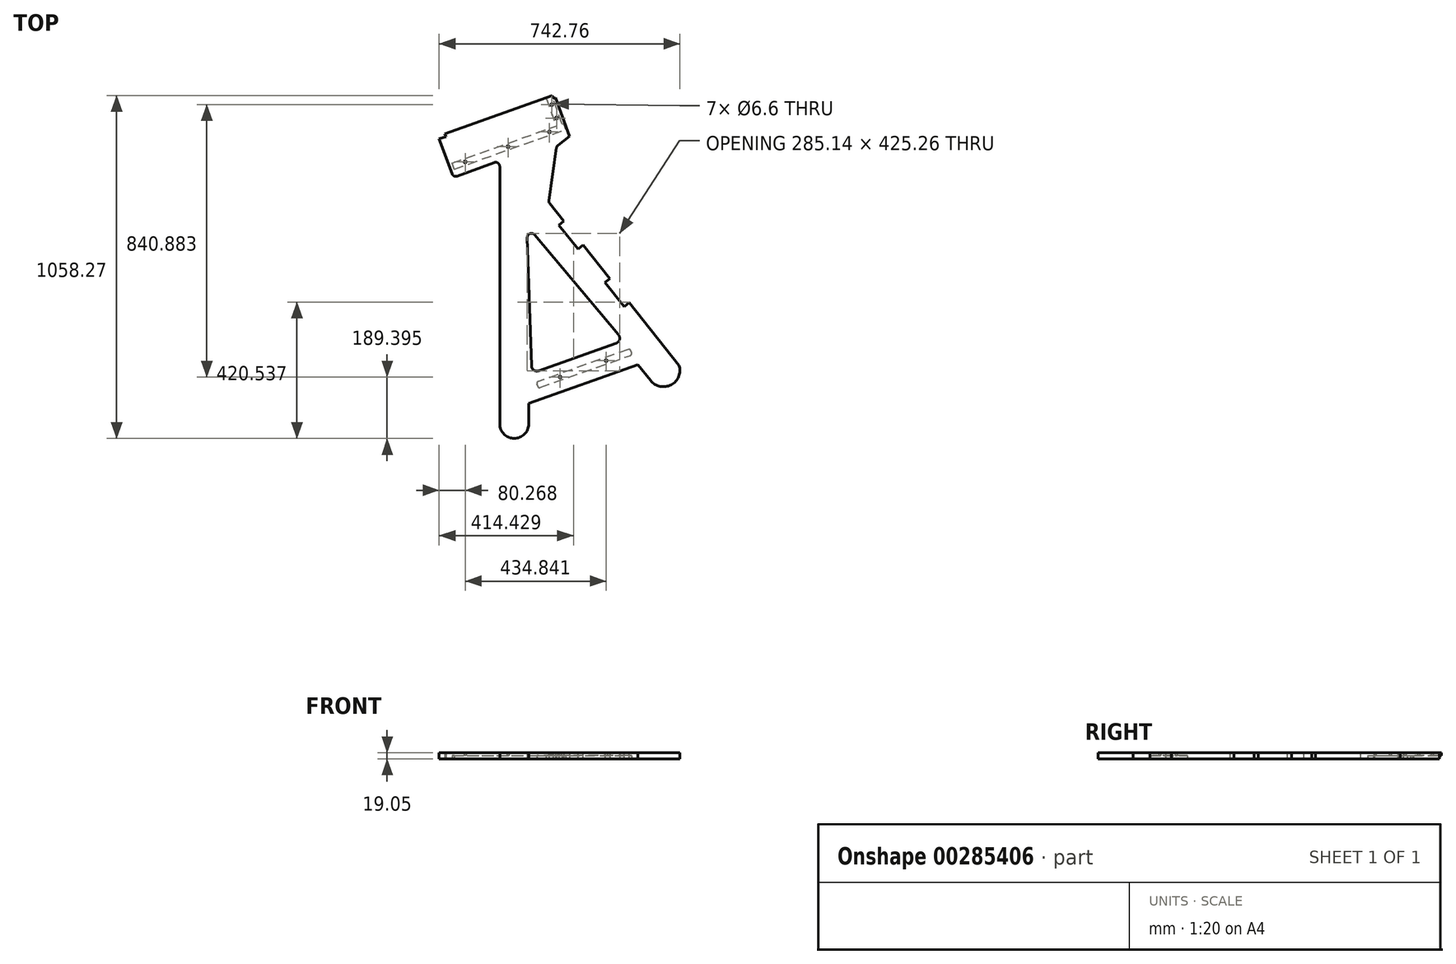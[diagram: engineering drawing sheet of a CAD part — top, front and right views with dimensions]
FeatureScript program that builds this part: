
annotation { "Feature Type Name" : "Feature", "Feature Type Description" : "" }
export const myFeature = defineFeature(function(context is Context, id is Id, definition is map)
    precondition{}
    {
        {
            var Q0;
            Q0=qCreatedBy(makeId("Top.planeOp"),FACE);
            var sketch = newSketch(context, id + "F0", { "sketchPlane" : qUnion([Q0])});
            skLineSegment(sketch, "E0", {"start": v(-306.62, -10.3) * mm, "end": v(-306.88, -10.27) * mm});
            skLineSegment(sketch, "E1", {"start": v(727.27, -283.58) * mm, "end": v(727.27, 427.9) * mm});
            skPoint(sketch, "E2.visualSharp", {"position": v(727.27, -334.1) * mm});
            skPoint(sketch, "E3.visualSharp", {"position": v(828.87, -334.66) * mm});
            skLineSegment(sketch, "E4", {"start": v(902.24, 568.5) * mm, "end": v(878.6, 406.65) * mm});
            skLineSegment(sketch, "E5", {"start": v(727.27, 427.9) * mm, "end": v(727.27, 511.3) * mm});
            skLineSegment(sketch, "E6", {"start": v(710.18, 523.22) * mm, "end": v(596.17, 481.24) * mm});
            skLineSegment(sketch, "E7", {"start": v(579.86, 488.77) * mm, "end": v(540.37, 596.03) * mm});
            skLineSegment(sketch, "E8", {"start": v(540.37, 596.03) * mm, "end": v(561.03, 603.39) * mm});
            skLineSegment(sketch, "E9", {"start": v(899.3, 723.83) * mm, "end": v(941.9, 604.19) * mm});
            skLineSegment(sketch, "E10", {"start": v(906.95, 576.64) * mm, "end": v(941.9, 604.19) * mm});
            skLineSegment(sketch, "E11", {"start": v(540.37, 596.03) * mm, "end": v(561.03, 603.39) * mm, "construction": true});
            skPoint(sketch, "E12.visualSharp", {"position": v(1175.92, -180.14) * mm});
            skLineSegment(sketch, "E13", {"start": v(825.1, -104.38) * mm, "end": v(812.23, 291.9) * mm});
            skLineSegment(sketch, "E14", {"start": v(834.65, 300.48) * mm, "end": v(1093.51, -8.04) * mm});
            skPoint(sketch, "E15.visualSharp", {"position": v(811.04, 328.62) * mm});
            skArc(sketch, "E15.filletArc", {"start": v(834.65, 300.48) * mm, "mid": v(820.38, 304.18) * mm, "end": v(812.23, 291.9) * mm});
            skLineSegment(sketch, "E16", {"start": v(584.25, 476.85) * mm, "end": v(941.9, 604.19) * mm, "construction": true});
            skLineSegment(sketch, "E17", {"start": v(573.37, 506.42) * mm, "end": v(591.31, 512.8) * mm, "construction": true});
            skLineSegment(sketch, "E18", {"start": v(881.25, 396.88) * mm, "end": v(1280.84, -102.55) * mm});
            skLineSegment(sketch, "E19", {"start": v(1185.54, -137.77) * mm, "end": v(1280.84, -102.55) * mm, "construction": true});
            skArc(sketch, "E20", {"start": v(1192.54, -149.45) * mm, "mid": v(1256.13, -162.6) * mm, "end": v(1280.84, -102.55) * mm});
            skLineSegment(sketch, "E21", {"start": v(816.46, -283.58) * mm, "end": v(816.46, -220.06) * mm});
            skLineSegment(sketch, "E22", {"start": v(923.23, 732.35) * mm, "end": v(1268.85, -238.36) * mm, "construction": true});
            skPoint(sketch, "E23.visualSharp", {"position": v(1185.54, -137.77) * mm});
            skPoint(sketch, "E24.visualSharp", {"position": v(877.8, 401.2) * mm});
            skArc(sketch, "E24.filletArc", {"start": v(878.6, 406.65) * mm, "mid": v(878.9, 401.5) * mm, "end": v(881.25, 396.88) * mm});
            skPoint(sketch, "E25.visualSharp", {"position": v(902.97, 573.5) * mm});
            skArc(sketch, "E25.filletArc", {"start": v(906.95, 576.64) * mm, "mid": v(903.81, 573.02) * mm, "end": v(902.24, 568.5) * mm});
            skArc(sketch, "E26.filletArc", {"start": v(727.27, 511.3) * mm, "mid": v(721.83, 521.72) * mm, "end": v(710.18, 523.22) * mm});
            skLineSegment(sketch, "E27", {"start": v(557.84, 612.36) * mm, "end": v(888.53, 730.1) * mm});
            skLineSegment(sketch, "E28", {"start": v(557.84, 612.36) * mm, "end": v(561.03, 603.39) * mm});
            skLineSegment(sketch, "E29", {"start": v(888.53, 730.1) * mm, "end": v(891.73, 721.13) * mm});
            skLineSegment(sketch, "E30.trimOffspring", {"start": v(891.73, 721.13) * mm, "end": v(899.3, 723.83) * mm, "construction": true});
            skLineSegment(sketch, "E31.trimOffspring", {"start": v(891.73, 721.13) * mm, "end": v(899.3, 723.83) * mm});
            skLineSegment(sketch, "E32", {"start": v(540.37, 596.03) * mm, "end": v(913.6, -417.7) * mm, "construction": true});
            skLineSegment(sketch, "E33", {"start": v(877.85, -320.58) * mm, "end": v(1232.27, -194.4) * mm, "construction": true});
            skLineSegment(sketch, "E34", {"start": v(816.46, -220.06) * mm, "end": v(1153.13, -100.19) * mm});
            skLineSegment(sketch, "E35", {"start": v(847.13, -119.4) * mm, "end": v(1086.4, -34.2) * mm});
            skArc(sketch, "E36", {"start": v(727.27, -283.58) * mm, "mid": v(771.86, -328.17) * mm, "end": v(816.46, -283.58) * mm});
            skPoint(sketch, "E37.visualSharp", {"position": v(584.25, 476.85) * mm});
            skArc(sketch, "E37.filletArc", {"start": v(579.86, 488.77) * mm, "mid": v(586.46, 481.63) * mm, "end": v(596.17, 481.24) * mm});
            skPoint(sketch, "E38.visualSharp", {"position": v(1108.78, -26.24) * mm});
            skArc(sketch, "E38.filletArc", {"start": v(1086.4, -34.2) * mm, "mid": v(1096.8, -22.98) * mm, "end": v(1093.51, -8.04) * mm});
            skPoint(sketch, "E39.visualSharp", {"position": v(825.83, -126.99) * mm});
            skArc(sketch, "E39.filletArc", {"start": v(825.1, -104.38) * mm, "mid": v(832.3, -117.5) * mm, "end": v(847.13, -119.4) * mm});
            skLineSegment(sketch, "E40", {"start": v(1153.13, -100.19) * mm, "end": v(1192.54, -149.45) * mm});
            skPoint(sketch, "E41", {"position": v(1256.13, -162.6) * mm});
            skSolve(sketch);
        }
        {
            var Q0;
            Q0=makeQuery(id+"F0.imprint","IMPRINT",FACE,{"disambiguationData":[TD([[makeQuery(id+"F0.imprint","IMPRINT",EDGE,{"derivedFrom":sQuery(id+"F0.wireOp",EDGE,"oAVC5DI8-kh1G-Qbfy-uwvq-Txyh6lFHP0Ui")}),1.0]])]});
            var Q1;
            Q1=makeQuery(id+"F0.imprint","IMPRINT",FACE,{"disambiguationData":[TD([[makeQuery(id+"F0.imprint","IMPRINT",EDGE,{"derivedFrom":sQuery(id+"F0.wireOp",EDGE,"E1")}),-1.0]])]});
            extrude(context, id + "F1", {"entities" : qUnion([Q0, Q1]), "depth" : 19.05 * mm});
        }
        {
            var Q0;
            {var subQ2=sQuery(id+"F0.wireOp",EDGE,"E1");Q0=makeQuery(id+"F0.imprint","IMPRINT",FACE,{"disambiguationData":[TD([[makeQuery(id+"F0.imprint","IMPRINT",EDGE,{"derivedFrom":subQ2}),-1.0]])]});}
            var sketch = newSketch(context, id + "F2", { "sketchPlane" : qUnion([Q0])});
            skLineSegment(sketch, "E42", {"start": v(852.3, -170.94) * mm, "end": v(1129.86, -72.11) * mm});
            skLineSegment(sketch, "E43", {"start": v(1123.5, -53.62) * mm, "end": v(845.93, -152.44) * mm});
            skLineSegment(sketch, "E44", {"start": v(1133.77, -64.18) * mm, "end": v(1131.67, -57.65) * mm});
            skLineSegment(sketch, "E45", {"start": v(844.12, -166.9) * mm, "end": v(842.02, -160.38) * mm});
            skPoint(sketch, "E46.visualSharp", {"position": v(846.13, -173.13) * mm});
            skArc(sketch, "E46.filletArc", {"start": v(844.12, -166.9) * mm, "mid": v(847.36, -170.65) * mm, "end": v(852.3, -170.94) * mm});
            skPoint(sketch, "E47.visualSharp", {"position": v(840.12, -154.51) * mm});
            skArc(sketch, "E47.filletArc", {"start": v(845.93, -152.44) * mm, "mid": v(842.36, -155.62) * mm, "end": v(842.02, -160.38) * mm});
            skPoint(sketch, "E48.visualSharp", {"position": v(1135.67, -70.04) * mm});
            skArc(sketch, "E48.filletArc", {"start": v(1129.86, -72.11) * mm, "mid": v(1133.43, -68.94) * mm, "end": v(1133.77, -64.18) * mm});
            skPoint(sketch, "E49.visualSharp", {"position": v(1129.66, -51.42) * mm});
            skArc(sketch, "E49.filletArc", {"start": v(1131.67, -57.65) * mm, "mid": v(1128.43, -53.9) * mm, "end": v(1123.5, -53.62) * mm});
            skSolve(sketch);
        }
        {
            var Q0;
            Q0 = qSketchRegion(id + "F2", true);
            extrude(context, id + "F3", {"entities" : qUnion([Q0]), "operationType" : NewBodyOperationType.REMOVE, "depth" : 9.52 * mm});
        }
        {
            var Q0;
            {var subQ2=sQuery(id+"F0.wireOp",EDGE,"E1");Q0=makeQuery(id+"F0.imprint","IMPRINT",FACE,{"disambiguationData":[TD([[makeQuery(id+"F0.imprint","IMPRINT",EDGE,{"derivedFrom":subQ2}),-1.0]])]});}
            var sketch = newSketch(context, id + "F4", { "sketchPlane" : qUnion([Q0])});
            skLineSegment(sketch, "E50.bottom", {"start": v(586.5, 502.94) * mm, "end": v(930.54, 625.43) * mm});
            skLineSegment(sketch, "E50.top", {"start": v(579.94, 521.37) * mm, "end": v(901.35, 635.8) * mm});
            skLineSegment(sketch, "E50.left", {"start": v(586.5, 502.94) * mm, "end": v(579.94, 521.37) * mm});
            skLineSegment(sketch, "E51", {"start": v(870.05, 723.7) * mm, "end": v(901.35, 635.8) * mm});
            skPoint(sketch, "E52.0", {"position": v(891.73, 721.13) * mm});
            skPoint(sketch, "E53.0", {"position": v(888.53, 730.1) * mm});
            skLineSegment(sketch, "E54", {"start": v(888.53, 730.1) * mm, "end": v(891.73, 721.13) * mm});
            skLineSegment(sketch, "E55", {"start": v(888.53, 730.1) * mm, "end": v(870.05, 723.7) * mm});
            skLineSegment(sketch, "E56", {"start": v(919.83, 642.19) * mm, "end": v(891.73, 721.13) * mm});
            skLineSegment(sketch, "E57", {"start": v(919.83, 642.19) * mm, "end": v(924.04, 643.68) * mm});
            skLineSegment(sketch, "E58", {"start": v(930.54, 625.43) * mm, "end": v(924.04, 643.68) * mm});
            skSolve(sketch);
        }
        {
            var Q0;
            Q0 = qSketchRegion(id + "F4", true);
            extrude(context, id + "F5", {"entities" : qUnion([Q0]), "operationType" : NewBodyOperationType.REMOVE, "depth" : 9.52 * mm});
        }
        {
            var Q0;
            Q0=makeQuery(id+"F1.opExtrude","SWEPT_FACE",FACE,{"disambiguationData":[OSD([sQuery(id+"F0.wireOp",EDGE,"E18")])]});
            var sketch = newSketch(context, id + "F6", { "sketchPlane" : qUnion([Q0])});
            skLineSegment(sketch, "E59", {"start": v(-310.5, 19.05) * mm, "end": v(-310.5, 0) * mm});
            skLineSegment(sketch, "E60", {"start": v(-310.5, 0) * mm, "end": v(-405.25, 0) * mm});
            skLineSegment(sketch, "E61", {"start": v(-405.25, 0) * mm, "end": v(-405.25, 19.05) * mm});
            skLineSegment(sketch, "E62", {"start": v(-405.25, 19.05) * mm, "end": v(-310.5, 19.05) * mm});
            skLineSegment(sketch, "E63", {"start": v(-537.62, 21.33) * mm, "end": v(-537.62, -0.7) * mm});
            skLineSegment(sketch, "E64", {"start": v(-537.62, -0.7) * mm, "end": v(-632.36, -0.7) * mm});
            skLineSegment(sketch, "E65", {"start": v(-632.36, -0.7) * mm, "end": v(-632.36, 21.33) * mm});
            skLineSegment(sketch, "E66", {"start": v(-632.36, 21.33) * mm, "end": v(-537.62, 21.33) * mm});
            skSolve(sketch);
        }
        {
            var Q0;
            Q0 = qSketchRegion(id + "F6", true);
            extrude(context, id + "F7", {"entities" : qUnion([Q0]), "operationType" : NewBodyOperationType.REMOVE, "oppositeDirection" : true, "depth" : 19.56 * mm});
        }
        {
            var Q0;
            Q0=makeQuery(id+"F0.imprint","IMPRINT",FACE,{"disambiguationData":[TD([[makeQuery(id+"F0.imprint","IMPRINT",EDGE,{"derivedFrom":sQuery(id+"F0.wireOp",EDGE,"E1")}),-1.0]])]});
            var sketch = newSketch(context, id + "F8", { "sketchPlane" : qUnion([Q0])});
            skLineSegment(sketch, "E67", {"start": v(916.91, 620.58) * mm, "end": v(879.28, 726.3) * mm, "construction": true});
            skLineSegment(sketch, "E68.0", {"start": v(919.83, 642.19) * mm, "end": v(891.73, 721.13) * mm});
            skCircle(sketch, "E69", {"center": v(902.66, 660.61) * mm, "radius": 3.3 * mm});
            skCircle(sketch, "E70", {"center": v(887.92, 702.1) * mm, "radius": 3.3 * mm});
            skLineSegment(sketch, "E71", {"start": v(921.57, 632.52) * mm, "end": v(583.89, 512.3) * mm, "construction": true});
            skCircle(sketch, "E72", {"center": v(880.54, 617.91) * mm, "radius": 3.3 * mm});
            skCircle(sketch, "E73", {"center": v(620.64, 525.38) * mm, "radius": 3.3 * mm});
            skCircle(sketch, "E74", {"center": v(752.73, 572.4) * mm, "radius": 3.3 * mm});
            skLineSegment(sketch, "E75.0", {"start": v(1133.77, -64.18) * mm, "end": v(1131.67, -57.65) * mm});
            skLineSegment(sketch, "E76.0", {"start": v(1123.5, -53.62) * mm, "end": v(845.93, -152.44) * mm});
            skLineSegment(sketch, "E77", {"start": v(1123.33, -64.1) * mm, "end": v(843.4, -163.77) * mm, "construction": true});
            skCircle(sketch, "E78", {"center": v(1055.48, -88.26) * mm, "radius": 3.3 * mm});
            skCircle(sketch, "E79", {"center": v(913.6, -138.78) * mm, "radius": 3.3 * mm});
            skLineSegment(sketch, "E80", {"start": v(752.73, 572.4) * mm, "end": v(620.64, 525.38) * mm});
            skSolve(sketch);
        }
        {
            var Q0;
            Q0 = qSketchRegion(id + "F8", true);
            extrude(context, id + "F9", {"entities" : qUnion([Q0]), "operationType" : NewBodyOperationType.REMOVE, "endBound" : BoundingType.THROUGH_ALL, "depth" : 25.4 * mm});
        }
    });
